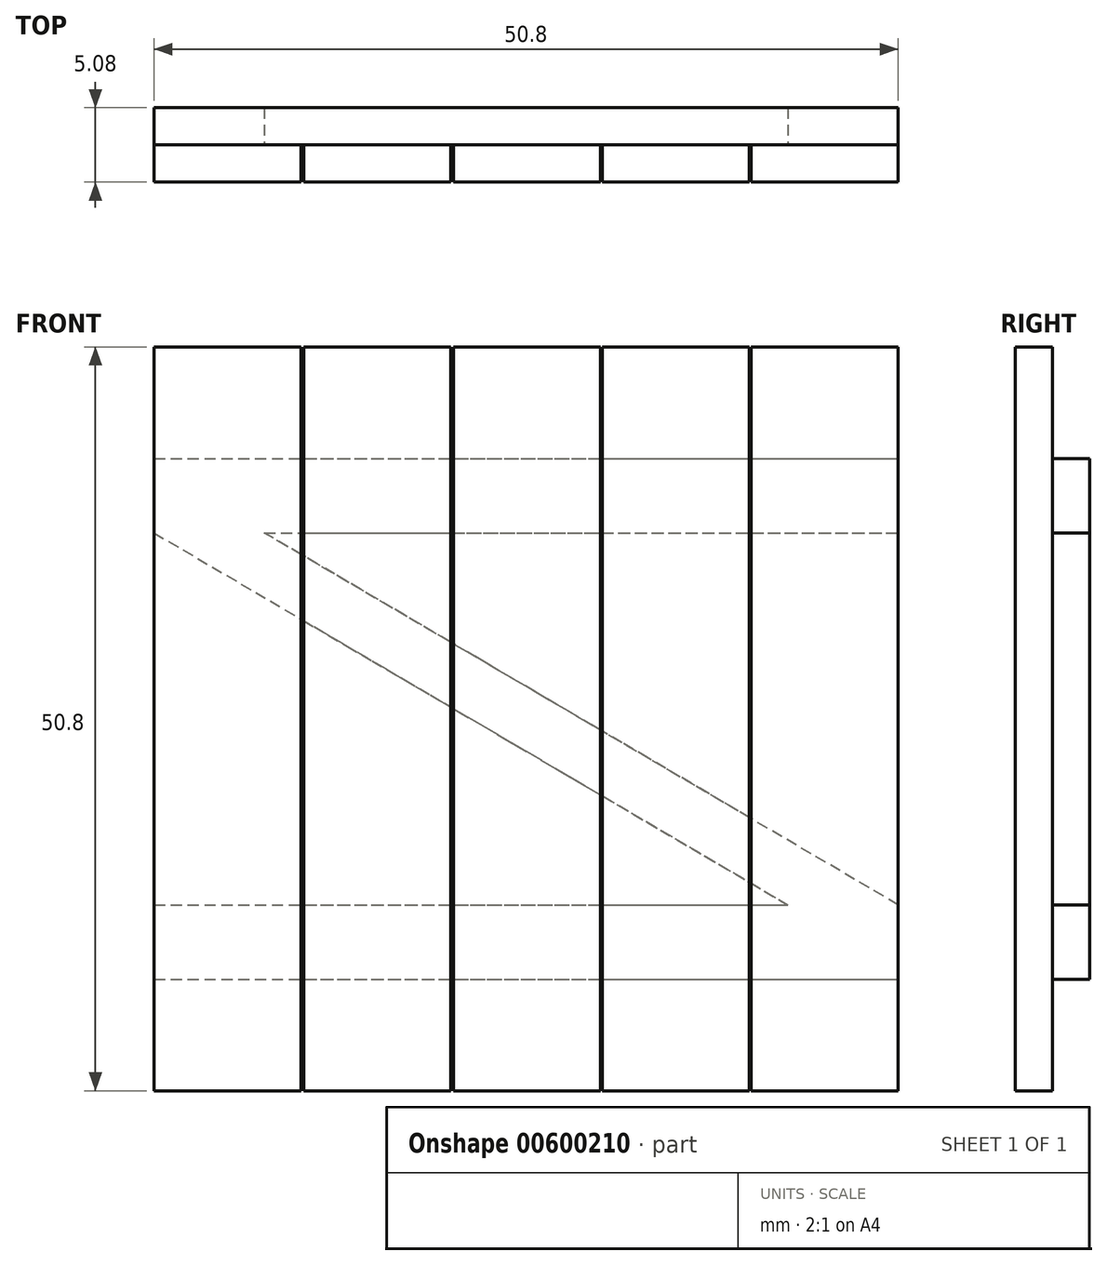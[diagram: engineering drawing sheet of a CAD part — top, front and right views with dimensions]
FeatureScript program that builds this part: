
annotation { "Feature Type Name" : "Feature", "Feature Type Description" : "" }
export const myFeature = defineFeature(function(context is Context, id is Id, definition is map)
    precondition{}
    {
        {
            var Q0;
            Q0=qCreatedBy(makeId("Front.planeOp"),FACE);
            var sketch = newSketch(context, id + "F0", { "sketchPlane" : qUnion([Q0])});
            skLineSegment(sketch, "E0.bottom", {"start": v(0, 0) * mm, "end": v(10.03, 0) * mm});
            skLineSegment(sketch, "E0.top", {"start": v(0, 50.8) * mm, "end": v(10.03, 50.8) * mm});
            skLineSegment(sketch, "E0.left", {"start": v(0, 0) * mm, "end": v(0, 50.8) * mm});
            skLineSegment(sketch, "E0.right", {"start": v(10.03, 0) * mm, "end": v(10.03, 50.8) * mm});
            skLineSegment(sketch, "E1.bottom", {"start": v(20.45, 0) * mm, "end": v(30.48, 0) * mm});
            skLineSegment(sketch, "E1.top", {"start": v(20.45, 50.8) * mm, "end": v(30.48, 50.8) * mm});
            skLineSegment(sketch, "E1.left", {"start": v(20.45, 0) * mm, "end": v(20.45, 50.8) * mm});
            skLineSegment(sketch, "E1.right", {"start": v(30.48, 0) * mm, "end": v(30.48, 50.8) * mm});
            skLineSegment(sketch, "E2.bottom", {"start": v(10.22, 0) * mm, "end": v(20.26, 0) * mm});
            skLineSegment(sketch, "E2.top", {"start": v(10.22, 50.8) * mm, "end": v(20.26, 50.8) * mm});
            skLineSegment(sketch, "E2.left", {"start": v(10.22, 0) * mm, "end": v(10.22, 50.8) * mm});
            skLineSegment(sketch, "E2.right", {"start": v(20.26, 0) * mm, "end": v(20.26, 50.8) * mm});
            skLineSegment(sketch, "E3.bottom", {"start": v(30.6, 0) * mm, "end": v(40.64, 0) * mm});
            skLineSegment(sketch, "E3.top", {"start": v(30.6, 50.8) * mm, "end": v(40.64, 50.8) * mm});
            skLineSegment(sketch, "E3.left", {"start": v(30.6, 0) * mm, "end": v(30.6, 50.8) * mm});
            skLineSegment(sketch, "E3.right", {"start": v(40.64, 0) * mm, "end": v(40.64, 50.8) * mm});
            skLineSegment(sketch, "E4.bottom", {"start": v(40.77, 0) * mm, "end": v(50.8, 0) * mm});
            skLineSegment(sketch, "E4.top", {"start": v(40.77, 50.8) * mm, "end": v(50.8, 50.8) * mm});
            skLineSegment(sketch, "E4.left", {"start": v(40.77, 0) * mm, "end": v(40.77, 50.8) * mm});
            skLineSegment(sketch, "E4.right", {"start": v(50.8, 0) * mm, "end": v(50.8, 50.8) * mm});
            skSolve(sketch);
        }
        {
            var Q0;
            Q0=makeQuery(id+"F0.imprint","IMPRINT",FACE,{"disambiguationData":[TD([[makeQuery(id+"F0.imprint","IMPRINT",EDGE,{"derivedFrom":sQuery(id+"F0.wireOp",EDGE,"E0.bottom")}),1.0]])]});
            var Q1;
            Q1=makeQuery(id+"F0.imprint","IMPRINT",FACE,{"disambiguationData":[TD([[makeQuery(id+"F0.imprint","IMPRINT",EDGE,{"derivedFrom":sQuery(id+"F0.wireOp",EDGE,"E1.bottom")}),1.0]])]});
            var Q2;
            Q2=makeQuery(id+"F0.imprint","IMPRINT",FACE,{"disambiguationData":[TD([[makeQuery(id+"F0.imprint","IMPRINT",EDGE,{"derivedFrom":sQuery(id+"F0.wireOp",EDGE,"E2.bottom")}),1.0]])]});
            var Q3;
            Q3=makeQuery(id+"F0.imprint","IMPRINT",FACE,{"disambiguationData":[TD([[makeQuery(id+"F0.imprint","IMPRINT",EDGE,{"derivedFrom":sQuery(id+"F0.wireOp",EDGE,"E3.bottom")}),1.0]])]});
            var Q4;
            Q4=makeQuery(id+"F0.imprint","IMPRINT",FACE,{"disambiguationData":[TD([[makeQuery(id+"F0.imprint","IMPRINT",EDGE,{"derivedFrom":sQuery(id+"F0.wireOp",EDGE,"E4.bottom")}),1.0]])]});
            extrude(context, id + "F1", {"entities" : qUnion([Q0, Q1, Q2, Q3, Q4]), "depth" : 2.54 * mm, "offsetDistance" : 25.4 * mm});
        }
        {
            var Q0;
            Q0=qCreatedBy(makeId("Front.planeOp"),FACE);
            var sketch = newSketch(context, id + "F2", { "sketchPlane" : qUnion([Q0])});
            skLineSegment(sketch, "E5.bottom", {"start": v(0, 7.62) * mm, "end": v(50.8, 7.62) * mm});
            skLineSegment(sketch, "E5.top", {"start": v(0, 12.7) * mm, "end": v(50.8, 12.7) * mm});
            skLineSegment(sketch, "E5.left", {"start": v(0, 7.62) * mm, "end": v(0, 12.7) * mm});
            skLineSegment(sketch, "E5.right", {"start": v(50.8, 7.62) * mm, "end": v(50.8, 12.7) * mm});
            skLineSegment(sketch, "E6.bottom", {"start": v(0, 38.1) * mm, "end": v(50.8, 38.1) * mm});
            skLineSegment(sketch, "E6.top", {"start": v(0, 43.18) * mm, "end": v(50.8, 43.18) * mm});
            skLineSegment(sketch, "E6.left", {"start": v(0, 38.1) * mm, "end": v(0, 43.18) * mm});
            skLineSegment(sketch, "E6.right", {"start": v(50.8, 38.1) * mm, "end": v(50.8, 43.18) * mm});
            skLineSegment(sketch, "E7", {"start": v(50.8, 12.7) * mm, "end": v(7.53, 38.1) * mm});
            skLineSegment(sketch, "E8", {"start": v(7.53, 38.1) * mm, "end": v(0, 38.1) * mm});
            skLineSegment(sketch, "E9", {"start": v(0, 38.1) * mm, "end": v(43.27, 12.7) * mm});
            skSolve(sketch);
        }
        {
            var Q0;
            Q0=makeQuery(id+"F2.imprint","IMPRINT",FACE,{"disambiguationData":[TD([[makeQuery(id+"F2.imprint","IMPRINT",EDGE,{"derivedFrom":sQuery(id+"F2.wireOp",EDGE,"E6.bottom")}),1.0]])]});
            var Q1;
            Q1=makeQuery(id+"F2.imprint","IMPRINT",FACE,{"disambiguationData":[TD([[makeQuery(id+"F2.imprint","IMPRINT",EDGE,{"derivedFrom":sQuery(id+"F2.wireOp",EDGE,"E5.bottom")}),1.0]])]});
            var Q2;
            {var subQ0=sQuery(id+"F2.wireOp",EDGE,"E7");Q2=makeQuery(id+"F2.imprint","IMPRINT",FACE,{"disambiguationData":[TD([[makeQuery(id+"F2.imprint","IMPRINT",EDGE,{"derivedFrom":subQ0}),1.0]])]});}
            extrude(context, id + "F3", {"entities" : qUnion([Q0, Q1, Q2]), "oppositeDirection" : true, "depth" : 2.54 * mm, "offsetDistance" : 25.4 * mm});
        }
    });
